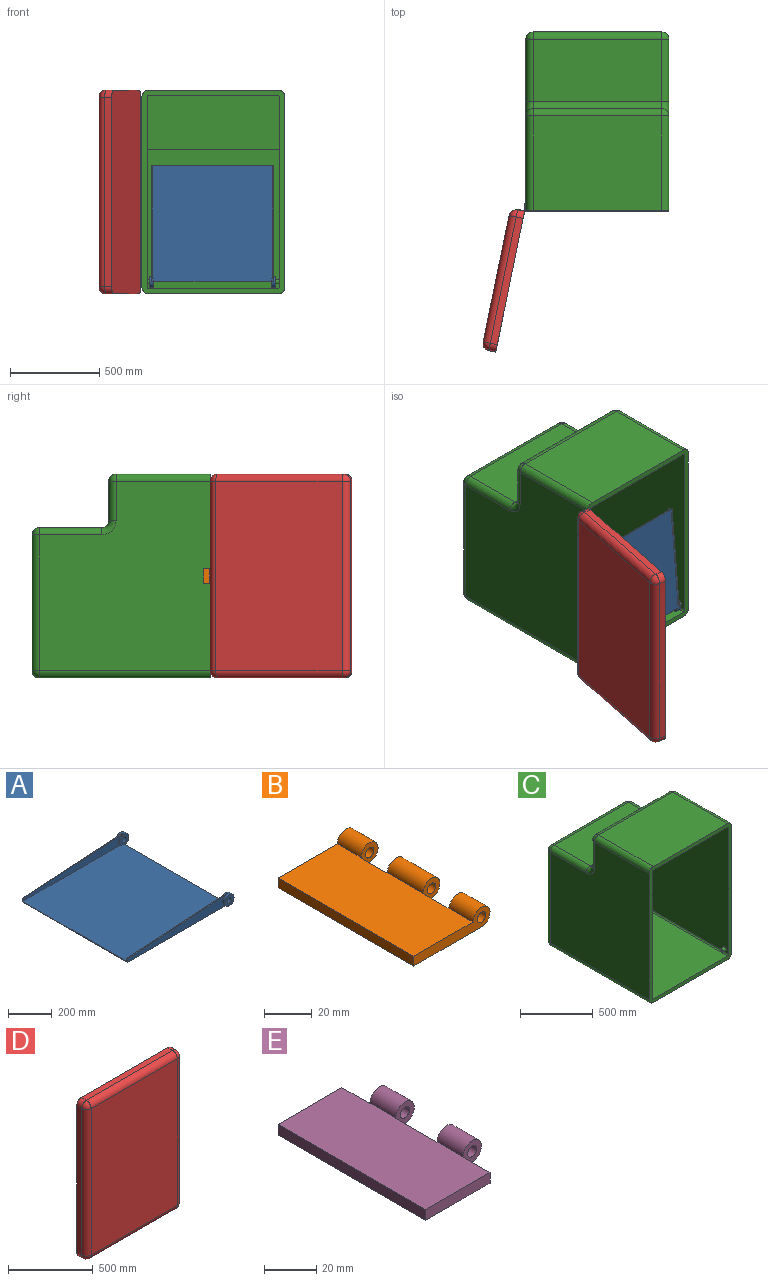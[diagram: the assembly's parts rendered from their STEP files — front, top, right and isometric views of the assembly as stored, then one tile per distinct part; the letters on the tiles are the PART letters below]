
ASSEMBLY  parts=5 mates=4
PART A: 21 faces, bbox 680x705x60 mm
  f0: plane 655x5mm, normal (1,0,0), area 3275mm2, adj f1,f9,f13,f18
  f1: plane 670x650mm, normal (0,0,1), area 435251.3mm2, adj f0,f4,f7,f8,f12,f13,f17,f18
  f2: plane 650x60mm, normal (0,-1,0), area 25036mm2, adj f4,f5,f9,f10,f12
  f3: plane 19.37x5mm, normal (0,0,1), area 96.9mm2, adj f6,f7,f11,f16
  f4: plane 680x20.2mm, normal (-1,0,0), area 3552mm2, adj f1,f2,f6,f7,f8,f9,f10,f11
  f5: plane 19.37x5mm, normal (0,0,1), area 96.9mm2, adj f2,f8,f10,f12
  f6: plane 650x60mm, normal (0,1,0), area 25036mm2, adj f3,f4,f9,f11,f16
  f7: plane 650x55mm, normal (0,-1,0), area 21842.3mm2, adj f1,f3,f4,f11,f17
  f8: plane 650x55mm, normal (0,1,0), area 21842.3mm2, adj f1,f4,f5,f10,f12
  f9: plane 680x650mm, normal (0,0,-1), area 442000mm2, adj f0,f2,f4,f6,f12,f16
  f10: plane 630.63x39.8mm, normal (-0.06,0,1), area 3159.4mm2, adj f2,f4,f5,f8
  f11: plane 630.63x39.8mm, normal (-0.06,0,1), area 3159.4mm2, adj f3,f4,f6,f7
  f12: cylinder r=30mm len=60mm, axis (0,-1,0), area 4109.4mm2, adj f1,f2,f5,f8,f9,f13,f14
  f13: plane 60x60mm, normal (0,1,0), area 2064.3mm2, adj f0,f1,f12,f15
  f14: plane 60x60mm, normal (0,-1,0), area 2120.6mm2, adj f12,f15
  f15: cylinder r=15mm len=30mm, axis (0,-1,0), area 2356.2mm2, adj f13,f14
  f16: cylinder r=30mm len=60mm, axis (0,-1,0), area 3534.3mm2, adj f3,f6,f9,f17,f18,f19
  f17: cylinder r=30mm len=55mm, axis (0,-1,0), area 575.1mm2, adj f1,f7,f16,f18
  f18: plane 60x60mm, normal (0,-1,0), area 2064.3mm2, adj f0,f1,f16,f17,f20
  f19: plane 60x60mm, normal (0,1,0), area 2120.6mm2, adj f16,f20
  f20: cylinder r=15mm len=30mm, axis (0,1,0), area 2356.2mm2, adj f18,f19
PART B: 17 faces, bbox 45x80x10 mm
  f0: plane 80x35mm, normal (0,0,1), area 2791.2mm2, adj f2,f3,f5,f6,f7,f8,f10,f11
  f1: plane 80x40mm, normal (0,0,-1), area 3036.2mm2, adj f2,f3,f5,f6,f7,f8,f10,f11
  f2: cylinder r=5mm len=21mm, axis (0,-1,0), area 494.8mm2, adj f0,f1,f11,f14
  f3: cylinder r=5mm len=14mm, axis (0,-1,0), area 329.9mm2, adj f0,f1,f5,f10
  f4: cylinder r=2.5mm len=14mm, axis (0,-1,0), area 219.9mm2, adj f5,f10
  f5: plane 45x10mm, normal (0,-1,0), area 239.3mm2, adj f0,f1,f3,f4,f7
  f6: plane 45x10mm, normal (0,1,0), area 239.3mm2, adj f0,f1,f7,f8,f9
  f7: plane 80x5mm, normal (-1,0,0), area 400mm2, adj f0,f1,f5,f6
  f8: cylinder r=5mm len=14mm, axis (0,-1,0), area 329.9mm2, adj f0,f1,f6,f13
  f9: cylinder r=2.5mm len=14mm, axis (0,-1,0), area 219.9mm2, adj f6,f13
  f10: plane 10.17x10mm, normal (0,1,0), area 65.1mm2, adj f0,f1,f3,f4,f12
  f11: plane 10.17x10mm, normal (0,-1,0), area 65.1mm2, adj f0,f1,f2,f12,f16
  f12: plane 15.5x5mm, normal (1,0,0), area 77.5mm2, adj f0,f1,f10,f11
  f13: plane 10.4x10mm, normal (0,-1,0), area 66.3mm2, adj f0,f1,f8,f9,f15
  f14: plane 10.4x10mm, normal (0,1,0), area 66.3mm2, adj f0,f1,f2,f15,f16
  f15: plane 15.5x5mm, normal (1,0,0), area 77.5mm2, adj f0,f1,f13,f14
  f16: cylinder r=2.5mm len=21mm, axis (0,-1,0), area 329.9mm2, adj f11,f14
PART C: 47 faces, bbox 800x1000x1140 mm
  f0: plane 1140x800mm, normal (0,-1,0), area 111512.4mm2, adj f1,f2,f3,f4,f5,f6,f7,f8
  f1: plane 720x530.58mm, normal (0,0,1), area 382019.9mm2, adj f0,f2,f8,f26
  f2: cylinder r=40mm len=530.58mm, axis (0,1,0), area 33337.5mm2, adj f0,f1,f3,f31
  f3: plane 1060x960mm, normal (-1,0,0), area 890148.4mm2, adj f0,f2,f4,f35,f36,f38,f40
  f4: cylinder r=40mm len=960mm, axis (0,1,0), area 60318.6mm2, adj f0,f3,f5,f32
  f5: plane 960x720mm, normal (0,0,-1), area 691200mm2, adj f0,f4,f6,f27
  f6: cylinder r=40mm len=960mm, axis (0,1,0), area 60318.6mm2, adj f0,f5,f7,f24
  f7: plane 1060x960mm, normal (1,0,0), area 890148.4mm2, adj f0,f6,f8,f25,f28,f29,f30
  f8: cylinder r=40mm len=530.58mm, axis (0,1,0), area 33337.5mm2, adj f0,f1,f7,f23
  f9: plane 760x720mm, normal (0,1,0), area 547200mm2, adj f27,f28,f36,f37
  f10: plane 720x349.42mm, normal (0,0,1), area 251580.1mm2, adj f29,f34,f37,f40
  f11: plane 720x220mm, normal (0,1,0), area 158400mm2, adj f25,f26,f34,f35
  f12: plane 720x540.58mm, normal (0,0,-1), area 389219.9mm2, adj f0,f13,f19,f22
  f13: cylinder r=10mm len=540.58mm, axis (0,1,0), area 8491.5mm2, adj f0,f12,f14,f22
  f14: plane 1060x970mm, normal (1,0,0), area 903053.4mm2, adj f0,f13,f15,f20,f21,f22,f41
  f15: cylinder r=10mm len=970mm, axis (0,1,0), area 15236.7mm2, adj f0,f14,f16,f20
  f16: plane 970x720mm, normal (0,0,1), area 698400mm2, adj f0,f15,f17,f20
  f17: cylinder r=10mm len=970mm, axis (0,1,0), area 15236.7mm2, adj f0,f16,f18,f20
  f18: plane 1060x970mm, normal (-1,0,0), area 903053.4mm2, adj f0,f17,f19,f20,f21,f22,f44
  f19: cylinder r=10mm len=540.58mm, axis (0,1,0), area 8491.5mm2, adj f0,f12,f18,f22
  f20: plane 780x740mm, normal (0,-1,0), area 577157.1mm2, adj f14,f15,f16,f17,f18,f21
  f21: plane 740x429.42mm, normal (0,0,-1), area 317768.5mm2, adj f14,f18,f20,f22
  f22: plane 740x300mm, normal (0,-1,0), area 221957.1mm2, adj f12,f13,f14,f18,f19,f21
  f23: sphere r=40mm, area 2513.3mm2, adj f8,f25,f26
  f24: sphere r=40mm, area 2513.3mm2, adj f6,f27,f28
  f25: cylinder r=40mm len=220mm, axis (0,0,1), area 13823mm2, adj f7,f11,f23,f30
  f26: cylinder r=40mm len=720mm, axis (-1,0,0), area 45238.9mm2, adj f1,f11,f23,f31
  f27: cylinder r=40mm len=720mm, axis (1,0,0), area 45238.9mm2, adj f5,f9,f24,f32
  f28: cylinder r=40mm len=760mm, axis (0,0,1), area 47752.2mm2, adj f7,f9,f24,f33
  f29: cylinder r=40mm len=349.42mm, axis (0,-1,0), area 21954.5mm2, adj f7,f10,f30,f33
  f30: torus R=80mm, axis (-1,0,0), area 5382.4mm2, adj f7,f25,f29,f34
  f31: sphere r=40mm, area 2513.3mm2, adj f2,f26,f35
  f32: sphere r=40mm, area 2513.3mm2, adj f4,f27,f36
  f33: sphere r=40mm, area 2513.3mm2, adj f28,f29,f37
  f34: cylinder r=40mm len=720mm, axis (1,0,0), area 45238.9mm2, adj f10,f11,f30,f38
  f35: cylinder r=40mm len=220mm, axis (0,0,-1), area 13823mm2, adj f3,f11,f31,f38
  f36: cylinder r=40mm len=760mm, axis (0,0,-1), area 47752.2mm2, adj f3,f9,f32,f39
  f37: cylinder r=40mm len=720mm, axis (-1,0,0), area 45238.9mm2, adj f9,f10,f33,f39
  f38: torus R=80mm, axis (-1,0,0), area 5382.4mm2, adj f3,f34,f35,f40
  f39: sphere r=40mm, area 2513.3mm2, adj f36,f37,f40
  f40: cylinder r=40mm len=349.42mm, axis (0,1,0), area 21954.5mm2, adj f3,f10,f38,f39
  f41: cylinder r=14mm len=30mm, axis (-1,0,0), area 2638.9mm2, adj f14,f43
  f42: plane 18x18mm, normal (1,0,0), area 254.5mm2, adj f43
  f43: cone r=9mm half-angle=45deg, axis (-1,0,0), area 510.9mm2, adj f41,f42
  f44: cylinder r=14mm len=30mm, axis (1,0,0), area 2638.9mm2, adj f18,f46
  f45: plane 18x18mm, normal (-1,0,0), area 254.5mm2, adj f46
  f46: cone r=9mm half-angle=45deg, axis (1,0,0), area 510.9mm2, adj f44,f45
PART D: 18 faces, bbox 800x80x1140 mm
  f0: plane 720x40mm, normal (0,0,1), area 28800mm2, adj f1,f7,f9,f14
  f1: cylinder r=40mm len=40mm, axis (0,1,0), area 2513.3mm2, adj f0,f2,f9,f12
  f2: plane 1060x40mm, normal (-1,0,0), area 42400mm2, adj f1,f3,f9,f10
  f3: cylinder r=40mm len=40mm, axis (0,1,0), area 2513.3mm2, adj f2,f4,f9,f11
  f4: plane 720x40mm, normal (0,0,-1), area 28800mm2, adj f3,f5,f9,f13
  f5: cylinder r=40mm len=40mm, axis (0,1,0), area 2513.3mm2, adj f4,f6,f9,f15
  f6: plane 1060x40mm, normal (1,0,0), area 42400mm2, adj f5,f7,f9,f17
  f7: cylinder r=40mm len=40mm, axis (0,1,0), area 2513.3mm2, adj f0,f6,f9,f16
  f8: plane 1060x720mm, normal (0,-1,0), area 763200mm2, adj f10,f13,f14,f17
  f9: plane 1140x800mm, normal (0,1,0), area 910626.5mm2, adj f0,f1,f2,f3,f4,f5,f6,f7
  f10: cylinder r=40mm len=1060mm, axis (0,0,1), area 66601.8mm2, adj f2,f8,f11,f12
  f11: sphere r=40mm, area 2513.3mm2, adj f3,f10,f13
  f12: sphere r=40mm, area 2513.3mm2, adj f1,f10,f14
  f13: cylinder r=40mm len=720mm, axis (-1,0,0), area 45238.9mm2, adj f4,f8,f11,f15
  f14: cylinder r=40mm len=720mm, axis (1,0,0), area 45238.9mm2, adj f0,f8,f12,f16
  f15: sphere r=40mm, area 2513.3mm2, adj f5,f13,f17
  f16: sphere r=40mm, area 2513.3mm2, adj f7,f14,f17
  f17: cylinder r=40mm len=1060mm, axis (0,0,-1), area 66601.8mm2, adj f6,f8,f15,f16
PART E: 16 faces, bbox 45x80x10 mm
  f0: plane 34.83x5mm, normal (0,-1,0), area 174.2mm2, adj f1,f5,f6,f12
  f1: plane 80x40mm, normal (0,0,-1), area 2922.7mm2, adj f0,f2,f3,f4,f5,f7,f8,f9
  f2: cylinder r=5mm len=14mm, axis (0,-1,0), area 329.9mm2, adj f1,f6,f7,f14
  f3: cylinder r=5mm len=14mm, axis (0,-1,0), area 329.9mm2, adj f1,f6,f8,f11
  f4: plane 34.6x5mm, normal (0,1,0), area 173mm2, adj f1,f5,f6,f13
  f5: plane 80x5mm, normal (-1,0,0), area 400mm2, adj f0,f1,f4,f6
  f6: plane 80x35mm, normal (0,0,1), area 2782.7mm2, adj f0,f2,f3,f4,f5,f7,f8,f9
  f7: plane 10.4x10mm, normal (0,-1,0), area 66.3mm2, adj f1,f2,f6,f9,f10
  f8: plane 10.4x10mm, normal (0,1,0), area 66.3mm2, adj f1,f3,f6,f9,f15
  f9: plane 22.4x5mm, normal (1,0,0), area 112mm2, adj f1,f6,f7,f8
  f10: cylinder r=2.5mm len=14mm, axis (0,-1,0), area 219.9mm2, adj f7,f14
  f11: plane 10.17x10mm, normal (0,-1,0), area 65.1mm2, adj f1,f3,f6,f12,f15
  f12: plane 14.8x5mm, normal (1,0,0), area 74mm2, adj f0,f1,f6,f11
  f13: plane 14.8x5mm, normal (1,0,0), area 74mm2, adj f1,f4,f6,f14
  f14: plane 10.4x10mm, normal (0,1,0), area 66.3mm2, adj f1,f2,f6,f10,f13
  f15: cylinder r=2.5mm len=14mm, axis (0,-1,0), area 219.9mm2, adj f8,f11
PLACE A rot(axis=(-0.59,0.59,0.54),122.9deg) t=(-296.97,292.1,-216.23)mm
PLACE B rot(axis=(0.58,-0.58,-0.58),120deg) t=(-1031.97,244.16,-353.9)mm
PLACE C t=(-631.97,1244.16,-313.9)mm fixed
PLACE D rot(axis=(0,0,-1),101.6deg) t=(-140.37,-353.21,-314.06)mm
PLACE E rot(axis=(-0.99,0.1,-0.1),90.6deg) t=(-1037.97,239.26,-274.1)mm
MATE fastened E.f1 <-> D.f2  axis (-0.2,-0.98,0) through (-1059.18,243.61,-314.06)mm
MATE revolute A.f12 <-> C.f43  axis (-1,0,0) through (-976.97,280.59,-816.49)mm
MATE fastened B.f1 <-> C.f3  axis (1,0,0) through (-1031.97,244.16,-313.9)mm
MATE revolute E.f2 <-> B.f2  axis (0,0,1) through (-1036.97,244.16,-288.9)mm
